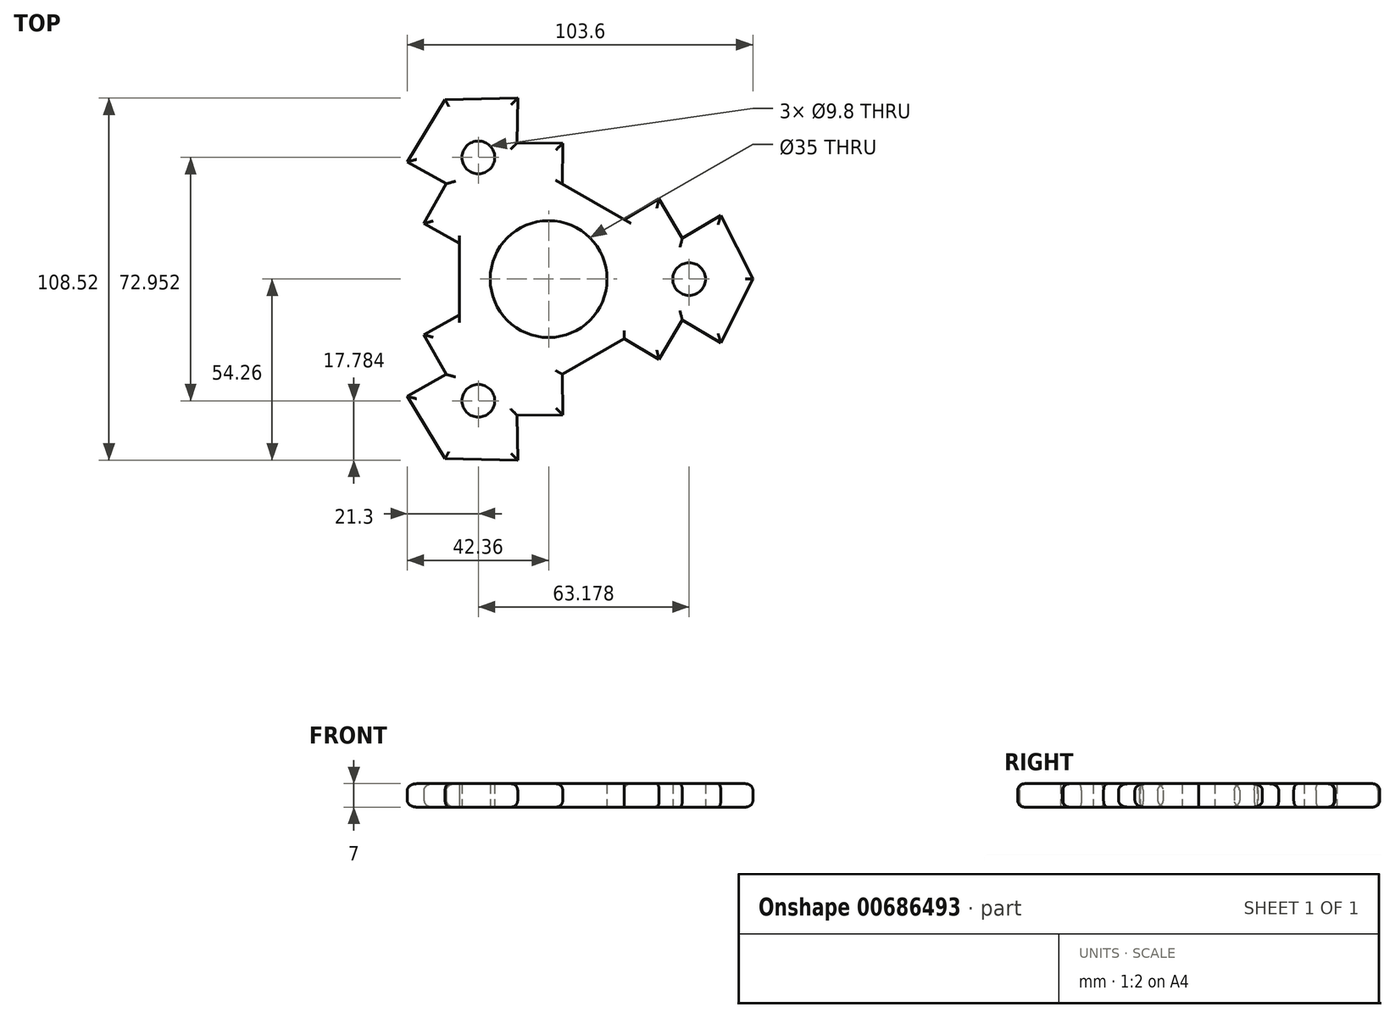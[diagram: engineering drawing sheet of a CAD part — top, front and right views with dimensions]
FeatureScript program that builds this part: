
annotation { "Feature Type Name" : "Feature", "Feature Type Description" : "" }
export const myFeature = defineFeature(function(context is Context, id is Id, definition is map)
    precondition{}
    {
        {
            var Q0;
            Q0=qCreatedBy(makeId("Top.planeOp"),FACE);
            var sketch = newSketch(context, id + "F0", { "sketchPlane" : qUnion([Q0])});
            skCircle(sketch, "E0", {"center": v(0, 0) * mm, "radius": 17.5 * mm});
            skCircle(sketch, "E1", {"center": v(0, 0) * mm, "radius": 11.15 * mm});
            skLineSegment(sketch, "E2", {"start": v(4.1, 28.51) * mm, "end": v(22.64, 17.8) * mm});
            skLineSegment(sketch, "E3", {"start": v(22.64, 17.8) * mm, "end": v(33.12, 24) * mm});
            skLineSegment(sketch, "E4", {"start": v(33.12, 24) * mm, "end": v(40.08, 12.27) * mm});
            skLineSegment(sketch, "E5", {"start": v(40.08, 12.27) * mm, "end": v(51.62, 19.1) * mm});
            skLineSegment(sketch, "E6", {"start": v(51.62, 19.1) * mm, "end": v(61.24, 0) * mm});
            skLineSegment(sketch, "E7.MirrorCS", {"start": v(4.1, -28.51) * mm, "end": v(22.64, -17.8) * mm});
            skLineSegment(sketch, "E8.MirrorCS", {"start": v(51.62, -19.1) * mm, "end": v(61.24, 0) * mm});
            skLineSegment(sketch, "E9.MirrorCS", {"start": v(33.12, -24) * mm, "end": v(40.08, -12.27) * mm});
            skLineSegment(sketch, "E10.MirrorCS", {"start": v(22.64, -17.8) * mm, "end": v(33.12, -24) * mm});
            skLineSegment(sketch, "E11.MirrorCS", {"start": v(40.08, -12.27) * mm, "end": v(51.62, -19.1) * mm});
            skLineSegment(sketch, "E12.1.0", {"start": v(-26.74, -10.7) * mm, "end": v(-26.74, 10.7) * mm});
            skLineSegment(sketch, "E12.1.1", {"start": v(-26.74, 10.7) * mm, "end": v(-37.35, 16.68) * mm});
            skLineSegment(sketch, "E12.1.2", {"start": v(-37.35, 16.68) * mm, "end": v(-30.66, 28.57) * mm});
            skLineSegment(sketch, "E12.1.3", {"start": v(-30.66, 28.57) * mm, "end": v(-42.36, 35.15) * mm});
            skLineSegment(sketch, "E12.1.4", {"start": v(-42.36, 35.15) * mm, "end": v(-31.03, 53.74) * mm});
            skLineSegment(sketch, "E12.1.5", {"start": v(-9.26, 54.26) * mm, "end": v(-31.03, 53.74) * mm});
            skLineSegment(sketch, "E12.1.6", {"start": v(-9.42, 40.84) * mm, "end": v(-9.26, 54.26) * mm});
            skLineSegment(sketch, "E12.1.7", {"start": v(4.23, 40.68) * mm, "end": v(-9.42, 40.84) * mm});
            skLineSegment(sketch, "E12.1.9", {"start": v(22.64, 17.8) * mm, "end": v(4.1, 28.51) * mm});
            skLineSegment(sketch, "E12.1.10", {"start": v(4.1, 28.51) * mm, "end": v(4.23, 40.68) * mm});
            skLineSegment(sketch, "E12.2.1", {"start": v(4.1, -28.51) * mm, "end": v(4.23, -40.68) * mm});
            skLineSegment(sketch, "E12.2.2", {"start": v(4.23, -40.68) * mm, "end": v(-9.42, -40.84) * mm});
            skLineSegment(sketch, "E12.2.3", {"start": v(-9.42, -40.84) * mm, "end": v(-9.26, -54.26) * mm});
            skLineSegment(sketch, "E12.2.4", {"start": v(-9.26, -54.26) * mm, "end": v(-31.03, -53.74) * mm});
            skLineSegment(sketch, "E12.2.5", {"start": v(-42.36, -35.15) * mm, "end": v(-31.03, -53.74) * mm});
            skLineSegment(sketch, "E12.2.6", {"start": v(-30.66, -28.57) * mm, "end": v(-42.36, -35.15) * mm});
            skLineSegment(sketch, "E12.2.7", {"start": v(-37.35, -16.68) * mm, "end": v(-30.66, -28.57) * mm});
            skLineSegment(sketch, "E12.2.9", {"start": v(-26.74, 10.7) * mm, "end": v(-26.74, -10.7) * mm});
            skLineSegment(sketch, "E12.2.10", {"start": v(-26.74, -10.7) * mm, "end": v(-37.35, -16.68) * mm});
            skCircle(sketch, "E13", {"center": v(42.12, 0) * mm, "radius": 4.9 * mm});
            skCircle(sketch, "E14.1.0", {"center": v(-21.06, 36.48) * mm, "radius": 4.9 * mm});
            skCircle(sketch, "E14.2.0", {"center": v(-21.06, -36.48) * mm, "radius": 4.9 * mm});
            skSolve(sketch);
        }
        {
            var Q0;
            Q0=makeQuery(id+"F0.imprint","IMPRINT",FACE,{"disambiguationData":[TD([[makeQuery(id+"F0.imprint","IMPRINT",EDGE,{"derivedFrom":sQuery(id+"F0.wireOp",EDGE,"E3")}),-1.0]])]});
            var Q1;
            Q1=makeQuery(id+"F0.imprint","IMPRINT",FACE,{"disambiguationData":[TD([[makeQuery(id+"F0.imprint","IMPRINT",EDGE,{"derivedFrom":sQuery(id+"F0.wireOp",EDGE,"E0")}),-1.0]])]});
            extrude(context, id + "F1", {"entities" : qUnion([Q0, Q1]), "depth" : 7 * mm, "offsetDistance" : 25 * mm});
        }
        {
            var Q0;
            Q0=makeQuery(id+"F1.opExtrude","CAP_EDGE",EDGE,{"disambiguationData":[OSD([sQuery(id+"F0.wireOp",EDGE,"E7.MirrorCS")])],"isStart":false});
            var Q1;
            Q1=makeQuery(id+"F1.opExtrude","CAP_EDGE",EDGE,{"disambiguationData":[OSD([sQuery(id+"F0.wireOp",EDGE,"E10.MirrorCS")])],"isStart":false});
            var Q2;
            Q2=makeQuery(id+"F1.opExtrude","CAP_EDGE",EDGE,{"disambiguationData":[OSD([sQuery(id+"F0.wireOp",EDGE,"E9.MirrorCS")])],"isStart":false});
            var Q3;
            Q3=makeQuery(id+"F1.opExtrude","CAP_EDGE",EDGE,{"disambiguationData":[OSD([sQuery(id+"F0.wireOp",EDGE,"E11.MirrorCS")])],"isStart":false});
            var Q4;
            Q4=makeQuery(id+"F1.opExtrude","CAP_EDGE",EDGE,{"disambiguationData":[OSD([sQuery(id+"F0.wireOp",EDGE,"E8.MirrorCS")])],"isStart":false});
            var Q5;
            Q5=makeQuery(id+"F1.opExtrude","CAP_EDGE",EDGE,{"disambiguationData":[OSD([sQuery(id+"F0.wireOp",EDGE,"E6")])],"isStart":false});
            var Q6;
            Q6=makeQuery(id+"F1.opExtrude","CAP_EDGE",EDGE,{"disambiguationData":[OSD([sQuery(id+"F0.wireOp",EDGE,"E5")])],"isStart":false});
            var Q7;
            Q7=makeQuery(id+"F1.opExtrude","CAP_EDGE",EDGE,{"disambiguationData":[OSD([sQuery(id+"F0.wireOp",EDGE,"E4")])],"isStart":false});
            var Q8;
            Q8=makeQuery(id+"F1.opExtrude","CAP_EDGE",EDGE,{"disambiguationData":[OSD([sQuery(id+"F0.wireOp",EDGE,"E3")])],"isStart":false});
            var Q9;
            Q9=makeQuery(id+"F1.opExtrude","CAP_EDGE",EDGE,{"disambiguationData":[OSD([sQuery(id+"F0.wireOp",EDGE,"E12.1.9")])],"isStart":false});
            var Q10;
            Q10=makeQuery(id+"F1.opExtrude","CAP_EDGE",EDGE,{"disambiguationData":[OSD([sQuery(id+"F0.wireOp",EDGE,"E12.1.10")])],"isStart":false});
            var Q11;
            Q11=makeQuery(id+"F1.opExtrude","CAP_EDGE",EDGE,{"disambiguationData":[OSD([sQuery(id+"F0.wireOp",EDGE,"E12.1.7")])],"isStart":false});
            var Q12;
            Q12=makeQuery(id+"F1.opExtrude","CAP_EDGE",EDGE,{"disambiguationData":[OSD([sQuery(id+"F0.wireOp",EDGE,"E12.1.6")])],"isStart":false});
            var Q13;
            Q13=makeQuery(id+"F1.opExtrude","CAP_EDGE",EDGE,{"disambiguationData":[OSD([sQuery(id+"F0.wireOp",EDGE,"E12.1.4")])],"isStart":false});
            var Q14;
            Q14=makeQuery(id+"F1.opExtrude","CAP_EDGE",EDGE,{"disambiguationData":[OSD([sQuery(id+"F0.wireOp",EDGE,"E12.1.5")])],"isStart":false});
            var Q15;
            Q15=makeQuery(id+"F1.opExtrude","CAP_EDGE",EDGE,{"disambiguationData":[OSD([sQuery(id+"F0.wireOp",EDGE,"E12.1.3")])],"isStart":false});
            var Q16;
            Q16=makeQuery(id+"F1.opExtrude","CAP_EDGE",EDGE,{"disambiguationData":[OSD([sQuery(id+"F0.wireOp",EDGE,"E12.1.2")])],"isStart":false});
            var Q17;
            Q17=makeQuery(id+"F1.opExtrude","CAP_EDGE",EDGE,{"disambiguationData":[OSD([sQuery(id+"F0.wireOp",EDGE,"E12.1.1")])],"isStart":false});
            var Q18;
            Q18=makeQuery(id+"F1.opExtrude","CAP_EDGE",EDGE,{"disambiguationData":[OSD([sQuery(id+"F0.wireOp",EDGE,"E12.2.9")])],"isStart":false});
            var Q19;
            Q19=makeQuery(id+"F1.opExtrude","CAP_EDGE",EDGE,{"disambiguationData":[OSD([sQuery(id+"F0.wireOp",EDGE,"E12.2.10")])],"isStart":false});
            var Q20;
            Q20=makeQuery(id+"F1.opExtrude","CAP_EDGE",EDGE,{"disambiguationData":[OSD([sQuery(id+"F0.wireOp",EDGE,"E12.2.7")])],"isStart":false});
            var Q21;
            Q21=makeQuery(id+"F1.opExtrude","CAP_EDGE",EDGE,{"disambiguationData":[OSD([sQuery(id+"F0.wireOp",EDGE,"E12.2.6")])],"isStart":false});
            var Q22;
            Q22=makeQuery(id+"F1.opExtrude","CAP_EDGE",EDGE,{"disambiguationData":[OSD([sQuery(id+"F0.wireOp",EDGE,"E12.2.5")])],"isStart":false});
            var Q23;
            Q23=makeQuery(id+"F1.opExtrude","CAP_EDGE",EDGE,{"disambiguationData":[OSD([sQuery(id+"F0.wireOp",EDGE,"E12.2.4")])],"isStart":false});
            var Q24;
            Q24=makeQuery(id+"F1.opExtrude","CAP_EDGE",EDGE,{"disambiguationData":[OSD([sQuery(id+"F0.wireOp",EDGE,"E12.2.2")])],"isStart":false});
            var Q25;
            Q25=makeQuery(id+"F1.opExtrude","CAP_EDGE",EDGE,{"disambiguationData":[OSD([sQuery(id+"F0.wireOp",EDGE,"E12.2.1")])],"isStart":false});
            var Q26;
            Q26=makeQuery(id+"F1.opExtrude","CAP_EDGE",EDGE,{"disambiguationData":[OSD([sQuery(id+"F0.wireOp",EDGE,"E12.2.3")])],"isStart":false});
            var Q27;
            Q27=makeQuery(id+"F1.opExtrude","CAP_EDGE",EDGE,{"disambiguationData":[OSD([sQuery(id+"F0.wireOp",EDGE,"E12.2.4")])],"isStart":true});
            var Q28;
            Q28=makeQuery(id+"F1.opExtrude","CAP_EDGE",EDGE,{"disambiguationData":[OSD([sQuery(id+"F0.wireOp",EDGE,"E12.2.5")])],"isStart":true});
            var Q29;
            Q29=makeQuery(id+"F1.opExtrude","CAP_EDGE",EDGE,{"disambiguationData":[OSD([sQuery(id+"F0.wireOp",EDGE,"E12.2.3")])],"isStart":true});
            var Q30;
            Q30=makeQuery(id+"F1.opExtrude","CAP_EDGE",EDGE,{"disambiguationData":[OSD([sQuery(id+"F0.wireOp",EDGE,"E12.2.2")])],"isStart":true});
            var Q31;
            Q31=makeQuery(id+"F1.opExtrude","CAP_EDGE",EDGE,{"disambiguationData":[OSD([sQuery(id+"F0.wireOp",EDGE,"E12.2.1")])],"isStart":true});
            var Q32;
            Q32=makeQuery(id+"F1.opExtrude","CAP_EDGE",EDGE,{"disambiguationData":[OSD([sQuery(id+"F0.wireOp",EDGE,"E7.MirrorCS")])],"isStart":true});
            var Q33;
            Q33=makeQuery(id+"F1.opExtrude","CAP_EDGE",EDGE,{"disambiguationData":[OSD([sQuery(id+"F0.wireOp",EDGE,"E10.MirrorCS")])],"isStart":true});
            var Q34;
            Q34=makeQuery(id+"F1.opExtrude","CAP_EDGE",EDGE,{"disambiguationData":[OSD([sQuery(id+"F0.wireOp",EDGE,"E9.MirrorCS")])],"isStart":true});
            var Q35;
            Q35=makeQuery(id+"F1.opExtrude","CAP_EDGE",EDGE,{"disambiguationData":[OSD([sQuery(id+"F0.wireOp",EDGE,"E11.MirrorCS")])],"isStart":true});
            var Q36;
            Q36=makeQuery(id+"F1.opExtrude","CAP_EDGE",EDGE,{"disambiguationData":[OSD([sQuery(id+"F0.wireOp",EDGE,"E8.MirrorCS")])],"isStart":true});
            var Q37;
            Q37=makeQuery(id+"F1.opExtrude","CAP_EDGE",EDGE,{"disambiguationData":[OSD([sQuery(id+"F0.wireOp",EDGE,"E6")])],"isStart":true});
            var Q38;
            Q38=makeQuery(id+"F1.opExtrude","CAP_EDGE",EDGE,{"disambiguationData":[OSD([sQuery(id+"F0.wireOp",EDGE,"E5")])],"isStart":true});
            var Q39;
            Q39=makeQuery(id+"F1.opExtrude","CAP_EDGE",EDGE,{"disambiguationData":[OSD([sQuery(id+"F0.wireOp",EDGE,"E4")])],"isStart":true});
            var Q40;
            Q40=makeQuery(id+"F1.opExtrude","CAP_EDGE",EDGE,{"disambiguationData":[OSD([sQuery(id+"F0.wireOp",EDGE,"E12.1.9")])],"isStart":true});
            var Q41;
            Q41=makeQuery(id+"F1.opExtrude","CAP_EDGE",EDGE,{"disambiguationData":[OSD([sQuery(id+"F0.wireOp",EDGE,"E12.1.10")])],"isStart":true});
            var Q42;
            Q42=makeQuery(id+"F1.opExtrude","CAP_EDGE",EDGE,{"disambiguationData":[OSD([sQuery(id+"F0.wireOp",EDGE,"E12.1.6")])],"isStart":true});
            var Q43;
            Q43=makeQuery(id+"F1.opExtrude","CAP_EDGE",EDGE,{"disambiguationData":[OSD([sQuery(id+"F0.wireOp",EDGE,"E12.1.7")])],"isStart":true});
            var Q44;
            Q44=makeQuery(id+"F1.opExtrude","CAP_EDGE",EDGE,{"disambiguationData":[OSD([sQuery(id+"F0.wireOp",EDGE,"E12.1.5")])],"isStart":true});
            var Q45;
            Q45=makeQuery(id+"F1.opExtrude","CAP_EDGE",EDGE,{"disambiguationData":[OSD([sQuery(id+"F0.wireOp",EDGE,"E12.2.6")])],"isStart":true});
            var Q46;
            Q46=makeQuery(id+"F1.opExtrude","CAP_EDGE",EDGE,{"disambiguationData":[OSD([sQuery(id+"F0.wireOp",EDGE,"E12.2.7")])],"isStart":true});
            var Q47;
            Q47=makeQuery(id+"F1.opExtrude","CAP_EDGE",EDGE,{"disambiguationData":[OSD([sQuery(id+"F0.wireOp",EDGE,"E12.2.10")])],"isStart":true});
            var Q48;
            Q48=makeQuery(id+"F1.opExtrude","CAP_EDGE",EDGE,{"disambiguationData":[OSD([sQuery(id+"F0.wireOp",EDGE,"E12.2.9")])],"isStart":true});
            var Q49;
            Q49=makeQuery(id+"F1.opExtrude","CAP_EDGE",EDGE,{"disambiguationData":[OSD([sQuery(id+"F0.wireOp",EDGE,"E12.1.1")])],"isStart":true});
            var Q50;
            Q50=makeQuery(id+"F1.opExtrude","CAP_EDGE",EDGE,{"disambiguationData":[OSD([sQuery(id+"F0.wireOp",EDGE,"E12.1.2")])],"isStart":true});
            var Q51;
            Q51=makeQuery(id+"F1.opExtrude","CAP_EDGE",EDGE,{"disambiguationData":[OSD([sQuery(id+"F0.wireOp",EDGE,"E12.1.3")])],"isStart":true});
            var Q52;
            Q52=makeQuery(id+"F1.opExtrude","CAP_EDGE",EDGE,{"disambiguationData":[OSD([sQuery(id+"F0.wireOp",EDGE,"E12.1.4")])],"isStart":true});
            fillet(context, id + "F2", {"entities" : qUnion([Q0, Q1, Q2, Q3, Q4, Q5, Q6, Q7, Q8, Q9, Q10, Q11, Q12, Q13, Q14, Q15, Q16, Q17, Q18, Q19, Q20, Q21, Q22, Q23, Q24, Q25, Q26, Q27, Q28, Q29, Q30, Q31, Q32, Q33, Q34, Q35, Q36, Q37, Q38, Q39, Q40, Q41, Q42, Q43, Q44, Q45, Q46, Q47, Q48, Q49, Q50, Q51, Q52]), "radius" : 2 * mm, "tangentPropagation" : true, "allowEdgeOverflow" : false});
        }
    });
